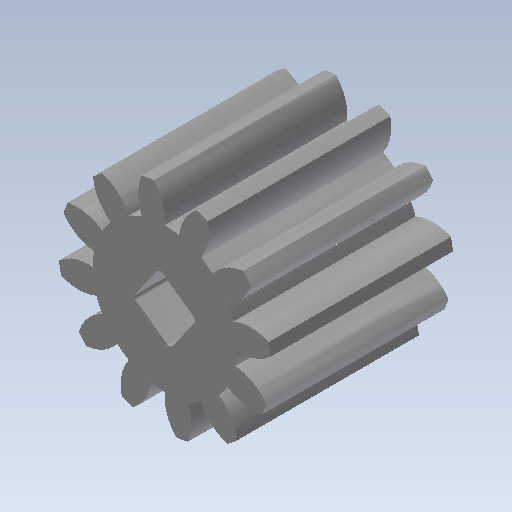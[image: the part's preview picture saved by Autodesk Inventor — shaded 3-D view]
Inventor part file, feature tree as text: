
AUTODESK INVENTOR PART (.ipt)
format: ipt  version: 2020 (Build 240168000, 168)  size: 201,216 bytes
history: native  units: in
note: dims shown in document units (in); Inventor stores cm internally (conversion verified against a paired STEP export)
features: extrude x2, sketch x2, other x1
ambient origin geometry x8: Origin, YZ Plane, XZ Plane, XY Plane, X Axis, Y Axis, Z Axis, Center Point
bodies: Solid1 (feature_tree)
feature tree (5):
  extrude  "Extrusion1"  Depth=0.5in TaperAngle=0.0deg
  sketch  "Sketch1"  dims[d0=0.5in d1=0.0in d2=1.0in d3=0.0in]
  sketch  "Sketch2"  dims[d4=0.0in d5=0.0in]
  other  "Srf1"
  extrude  "ExtrusionSrf1"  TaperAngle=0.0deg  [1 undecoded]
note: 1 required parameter value undecoded (feature->parameter linkage not recoverable at this tier; creation-order binding heuristic only, values carry confidence <= 0.55)
